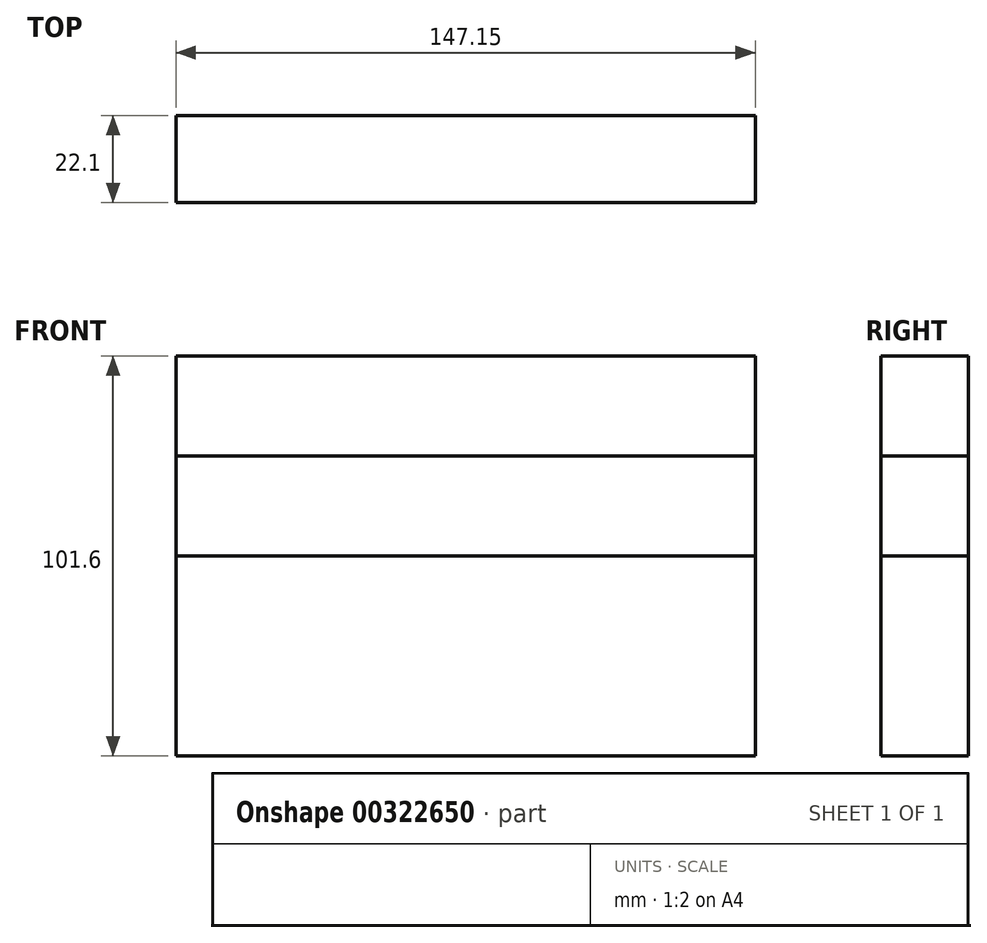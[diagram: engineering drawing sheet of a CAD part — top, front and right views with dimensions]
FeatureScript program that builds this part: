
annotation { "Feature Type Name" : "Feature", "Feature Type Description" : "" }
export const myFeature = defineFeature(function(context is Context, id is Id, definition is map)
    precondition{}
    {
        {
            var Q0;
            Q0=qCreatedBy(makeId("Top.planeOp"),FACE);
            var sketch = newSketch(context, id + "F0", { "sketchPlane" : qUnion([Q0])});
            skLineSegment(sketch, "E0.bottom", {"start": v(-72.8, 15.1) * mm, "end": v(74.35, 15.1) * mm});
            skLineSegment(sketch, "E0.top", {"start": v(-72.8, -7) * mm, "end": v(74.35, -7) * mm});
            skLineSegment(sketch, "E0.left", {"start": v(-72.8, 15.1) * mm, "end": v(-72.8, -7) * mm});
            skLineSegment(sketch, "E0.right", {"start": v(74.35, 15.1) * mm, "end": v(74.35, -7) * mm});
            skSolve(sketch);
        }
        {
            var Q0;
            Q0 = qSketchRegion(id + "F0", true);
            extrude(context, id + "F1", {"entities" : qUnion([Q0]), "depth" : 25.4 * mm});
        }
        {
            var Q0;
            Q0=makeQuery(id+"F1.opExtrude","CAP_FACE",FACE,{"disambiguationData":[OSD([sQuery(id+"F0.wireOp",EDGE,"E0.bottom"),sQuery(id+"F0.wireOp",EDGE,"E0.top"),sQuery(id+"F0.wireOp",EDGE,"E0.left"),sQuery(id+"F0.wireOp",EDGE,"E0.right")])],"isStart":false});
            extrude(context, id + "F2", {"entities" : qUnion([Q0]), "operationType" : NewBodyOperationType.ADD, "depth" : 25.4 * mm});
        }
        {
            var Q0;
            Q0=makeQuery(id+"F2.opExtrude","CAP_FACE",FACE,{"disambiguationData":[OSD([sQuery(id+"F0.wireOp",EDGE,"E0.bottom"),sQuery(id+"F0.wireOp",EDGE,"E0.top"),sQuery(id+"F0.wireOp",EDGE,"E0.left"),sQuery(id+"F0.wireOp",EDGE,"E0.right")])],"isStart":false});
            extrude(context, id + "F3", {"entities" : qUnion([Q0]), "depth" : 25.4 * mm});
        }
        {
            var Q0;
            Q0=makeQuery(id+"F3.opExtrude","CAP_FACE",FACE,{"disambiguationData":[OSD([sQuery(id+"F0.wireOp",EDGE,"E0.bottom"),sQuery(id+"F0.wireOp",EDGE,"E0.top"),sQuery(id+"F0.wireOp",EDGE,"E0.left"),sQuery(id+"F0.wireOp",EDGE,"E0.right")])],"isStart":false});
            extrude(context, id + "F4", {"entities" : qUnion([Q0]), "depth" : 25.4 * mm});
        }
    });
